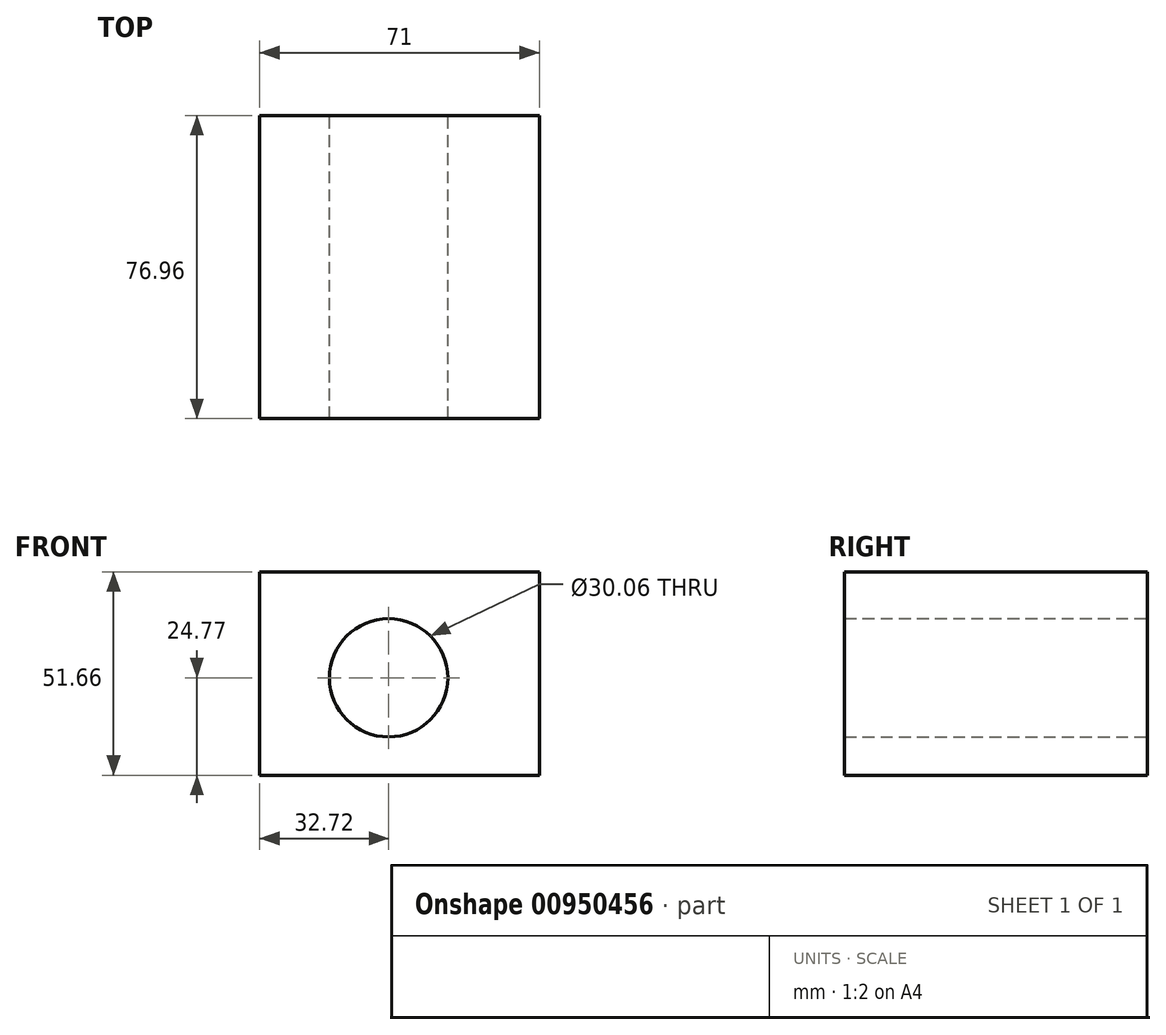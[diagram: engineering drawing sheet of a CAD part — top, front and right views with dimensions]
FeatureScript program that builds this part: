
annotation { "Feature Type Name" : "Feature", "Feature Type Description" : "" }
export const myFeature = defineFeature(function(context is Context, id is Id, definition is map)
    precondition{}
    {
        {
            var Q0;
            Q0=qCreatedBy(makeId("Front.planeOp"),FACE);
            var sketch = newSketch(context, id + "F0", { "sketchPlane" : qUnion([Q0])});
            skLineSegment(sketch, "E0.bottom", {"start": v(-32.72, 26.9) * mm, "end": v(38.28, 26.9) * mm});
            skLineSegment(sketch, "E0.top", {"start": v(-32.72, -24.77) * mm, "end": v(38.28, -24.77) * mm});
            skLineSegment(sketch, "E0.left", {"start": v(-32.72, 26.9) * mm, "end": v(-32.72, -24.77) * mm});
            skLineSegment(sketch, "E0.right", {"start": v(38.28, 26.9) * mm, "end": v(38.28, -24.77) * mm});
            skCircle(sketch, "E1", {"center": v(0, 0) * mm, "radius": 15.03 * mm});
            skSolve(sketch);
        }
        {
            var Q0;
            Q0=makeQuery(id+"F0.imprint","IMPRINT",FACE,{"disambiguationData":[TD([[makeQuery(id+"F0.imprint","IMPRINT",EDGE,{"derivedFrom":sQuery(id+"F0.wireOp",EDGE,"E0.bottom")}),-1.0]])]});
            extrude(context, id + "F1", {"entities" : qUnion([Q0]), "depth" : 76.96 * mm, "offsetDistance" : 25.4 * mm});
        }
    });
